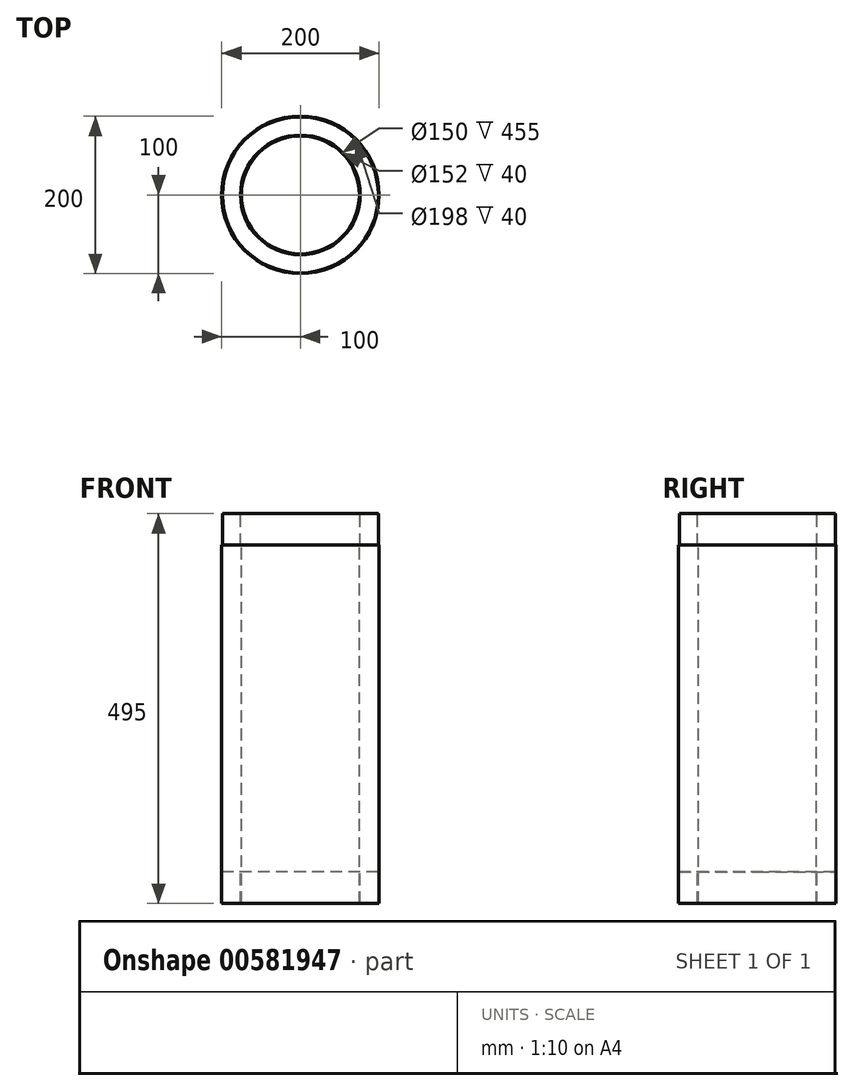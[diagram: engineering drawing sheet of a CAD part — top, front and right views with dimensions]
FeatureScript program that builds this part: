
annotation { "Feature Type Name" : "Feature", "Feature Type Description" : "" }
export const myFeature = defineFeature(function(context is Context, id is Id, definition is map)
    precondition{}
    {
        {
            var Q0;
            Q0=qCreatedBy(makeId("Front.planeOp"),FACE);
            var sketch = newSketch(context, id + "F0", { "sketchPlane" : qUnion([Q0])});
            skLineSegment(sketch, "E0", {"start": v(0, 345.75) * mm, "end": v(0, -558.03) * mm, "construction": true});
            skLineSegment(sketch, "E1", {"start": v(-75, -518.84) * mm, "end": v(-75, -63.84) * mm});
            skLineSegment(sketch, "E2", {"start": v(-75, -63.84) * mm, "end": v(-76, -63.84) * mm});
            skLineSegment(sketch, "E3", {"start": v(-76, -63.84) * mm, "end": v(-76, -23.84) * mm});
            skLineSegment(sketch, "E4", {"start": v(-76, -23.84) * mm, "end": v(-99, -23.84) * mm});
            skLineSegment(sketch, "E5", {"start": v(-99, -23.84) * mm, "end": v(-99, -63.84) * mm});
            skLineSegment(sketch, "E6", {"start": v(-99, -63.84) * mm, "end": v(-100, -63.84) * mm});
            skLineSegment(sketch, "E7", {"start": v(-100, -63.84) * mm, "end": v(-100, -518.84) * mm});
            skLineSegment(sketch, "E8", {"start": v(-100, -518.84) * mm, "end": v(-99, -518.84) * mm});
            skLineSegment(sketch, "E9", {"start": v(-99, -518.84) * mm, "end": v(-99, -478.84) * mm});
            skLineSegment(sketch, "E10", {"start": v(-99, -478.84) * mm, "end": v(-76, -478.84) * mm});
            skLineSegment(sketch, "E11", {"start": v(-76, -478.84) * mm, "end": v(-76, -518.84) * mm});
            skLineSegment(sketch, "E12", {"start": v(-76, -518.84) * mm, "end": v(-75, -518.84) * mm});
            skSolve(sketch);
        }
        {
            var Q0;
            Q0=qSketchRegion(id+"F0",true);
            var Q1;
            Q1=sQuery(id+"F0.wireOp",EDGE,"E0");
            revolve(context, id + "F1", {"entities" : qUnion([Q0]), "axis" : qUnion([Q1]), "revolveType" : RevolveType.FULL});
        }
    });
